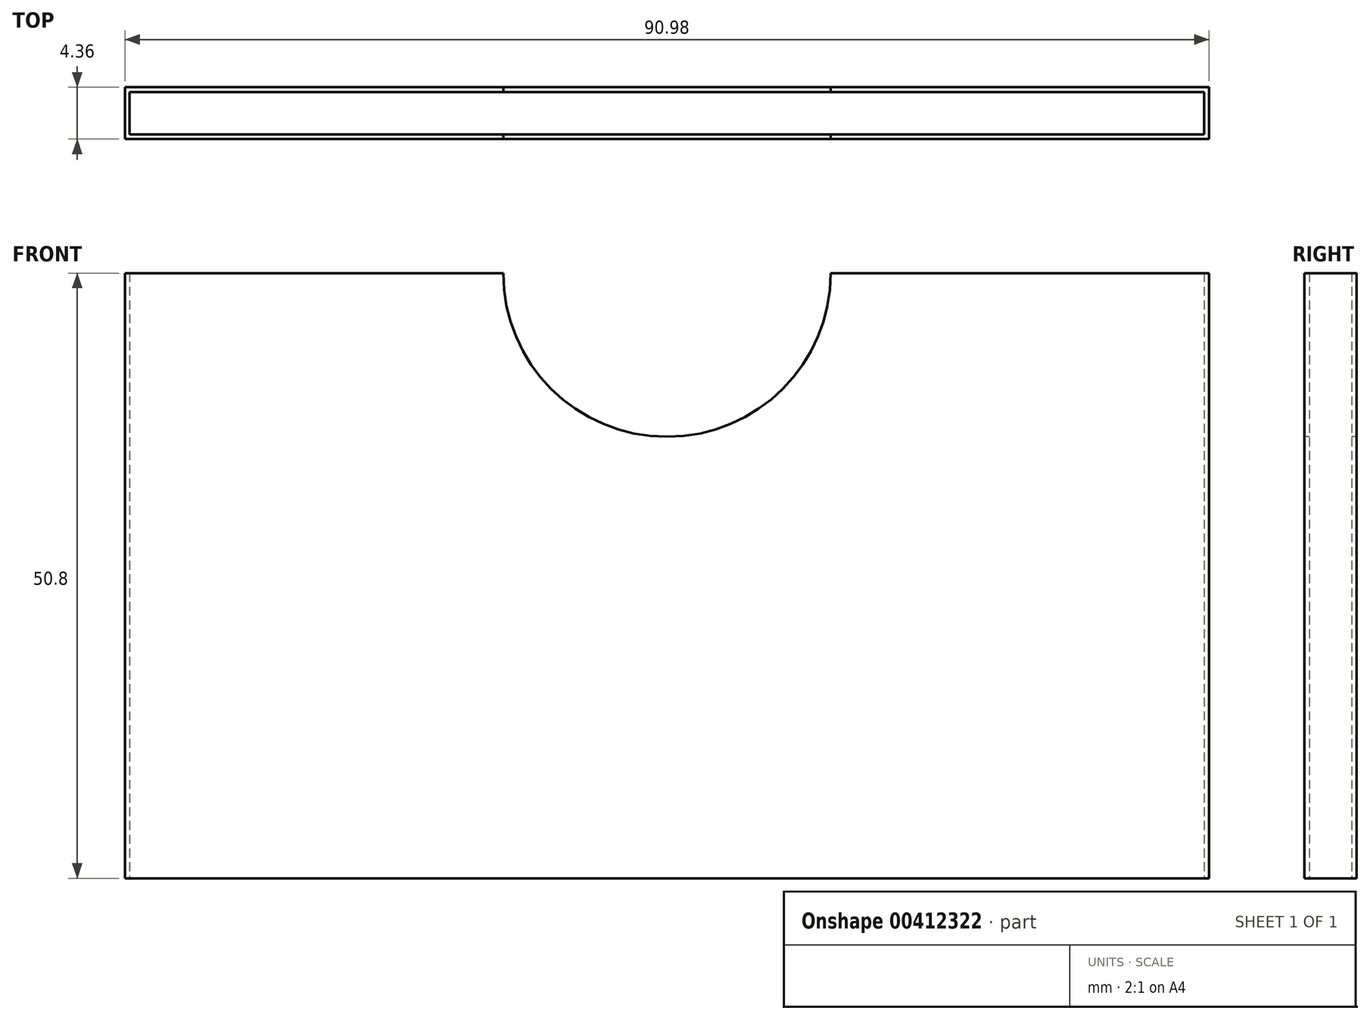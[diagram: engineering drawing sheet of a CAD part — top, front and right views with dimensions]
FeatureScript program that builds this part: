
annotation { "Feature Type Name" : "Feature", "Feature Type Description" : "" }
export const myFeature = defineFeature(function(context is Context, id is Id, definition is map)
    precondition{}
    {
        {
            var Q0;
            Q0=qCreatedBy(makeId("Top.planeOp"),FACE);
            var sketch = newSketch(context, id + "F0", { "sketchPlane" : qUnion([Q0])});
            skLineSegment(sketch, "E0.bottom", {"start": v(45.09, 1.78) * mm, "end": v(-45.09, 1.78) * mm});
            skLineSegment(sketch, "E0.top", {"start": v(45.09, -1.78) * mm, "end": v(-45.09, -1.78) * mm});
            skLineSegment(sketch, "E0.left", {"start": v(45.09, 1.78) * mm, "end": v(45.09, -1.78) * mm});
            skLineSegment(sketch, "E0.right", {"start": v(-45.09, 1.78) * mm, "end": v(-45.09, -1.78) * mm});
            skPoint(sketch, "E0.middle", {"position": v(0, 0) * mm});
            skLineSegment(sketch, "E1.bottom", {"start": v(-45.5, 2.18) * mm, "end": v(45.5, 2.18) * mm});
            skLineSegment(sketch, "E1.top", {"start": v(-45.5, -2.18) * mm, "end": v(45.5, -2.18) * mm});
            skLineSegment(sketch, "E1.left", {"start": v(-45.5, 2.18) * mm, "end": v(-45.5, -2.18) * mm});
            skLineSegment(sketch, "E1.right", {"start": v(45.5, 2.18) * mm, "end": v(45.5, -2.18) * mm});
            skSolve(sketch);
        }
        {
            var Q0;
            Q0=qSketchRegion(id+"F0",true);
            extrude(context, id + "F1", {"entities" : qUnion([Q0]), "depth" : 50.8 * mm});
        }
        {
            var Q0;
            Q0=makeQuery(id+"F1.opExtrude","SWEPT_FACE",FACE,{"disambiguationData":[OSD([sQuery(id+"F0.wireOp",EDGE,"E1.top")])]});
            var sketch = newSketch(context, id + "F2", { "sketchPlane" : qUnion([Q0])});
            skArc(sketch, "E2", {"start": v(-13.74, 50.8) * mm, "mid": v(0, 37.06) * mm, "end": v(13.74, 50.8) * mm});
            skLineSegment(sketch, "E3", {"start": v(-45.5, 25.4) * mm, "end": v(45.5, 25.4) * mm, "construction": true});
            skArc(sketch, "E4.MirrorCS", {"start": v(-13.74, 0) * mm, "mid": v(0, 13.74) * mm, "end": v(13.74, 0) * mm});
            skSolve(sketch);
        }
        {
            var Q0;
            {var subQ0=sQuery(id+"F2.wireOp",EDGE,"E2");Q0=makeQuery(id+"F2.imprint","IMPRINT",FACE,{"disambiguationData":[TD([[makeQuery(id+"F2.imprint","IMPRINT",EDGE,{"derivedFrom":subQ0}),1.0]])]});}
            extrude(context, id + "F3", {"entities" : qUnion([Q0]), "operationType" : NewBodyOperationType.REMOVE, "endBound" : BoundingType.THROUGH_ALL, "oppositeDirection" : true, "depth" : 25.4 * mm});
        }
    });
